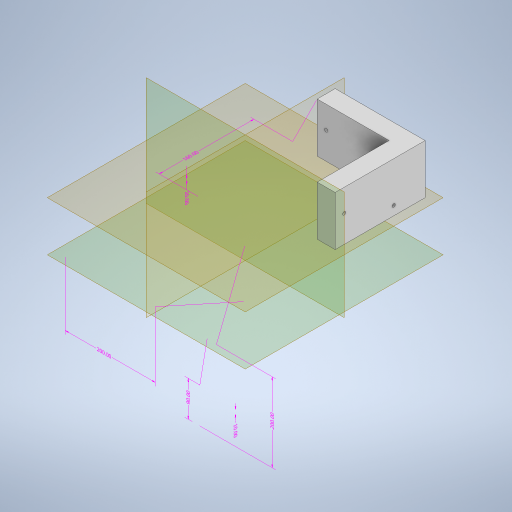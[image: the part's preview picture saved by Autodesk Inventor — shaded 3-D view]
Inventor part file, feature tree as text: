
AUTODESK INVENTOR PART (.ipt)
format: ipt  version: 2023 (Build 270158000, 158)  size: 439,808 bytes
history: native  units: mm
features: sketch x9, other x8, extrude x5, hole x4, plane x4, split x4
ambient origin geometry x8: Origin, YZ Plane, XZ Plane, XY Plane, X Axis, Y Axis, Z Axis, Center Point
bodies: Body1 (feature_tree)
feature tree (34):
  other  "Sólido1"
  other  "Anotaciones"
  extrude  "Extrusión1"  Depth=200.0mm
  hole  "Agujero1"  [1 undecoded]
  extrude  "Extrusión2"  Depth=15.0mm
  extrude  "Extrusión3"  Depth=80.0mm TaperAngle=0.0deg
  extrude  "Extrusión4"  Depth=200.0mm
  extrude  "Extrusión5"  Depth=20.0mm
  hole  "Agujero2"  [1 undecoded]
  plane  "Plano de trabajo1"
  split  "Dividir1"
  plane  "Plano de trabajo2"
  plane  "Plano de trabajo3"
  plane  "Plano de trabajo4"
  hole  "Agujero3"  [1 undecoded]
  hole  "Agujero4"  [1 undecoded]
  split  "Dividir2"
  split  "Dividir3"
  split  "Dividir4"
  sketch  "Boceto2"  dims[d7=15.0mm d8=200.0mm]
  sketch  "Boceto3"  dims[d9=10.0mm d10=0.0mm]
  sketch  "Boceto4"  dims[d11=3.5mm d12=1.75mm d13=1.75mm d14=1.75mm d15=1.75mm d16=10.0mm d17=10.0mm d19=40.0mm]
  sketch  "Boceto5"  dims[d20=3.5mm d21=6.0mm d22=4.0mm d23=2.0mm d24=90.0deg d25=8.0mm d26=20.594885mm d27=15.0mm]
  sketch  "Boceto6"  dims[d28=20.0mm d29=80.0mm d30=0.0mm]
  sketch  "Boceto7"  dims[d31=57.0mm d32=200.0mm]
  sketch  "Boceto8"  dims[d33=110.0mm d34=0.0mm d36=20.0mm]
  sketch  "Boceto9"  dims[d37=20.0mm d38=20.0mm]
  sketch  "Boceto10"  dims[d39=90.0mm d40=0.0mm d43=30.0mm d44=0.0mm d45=3.5mm d46=1.75mm d47=1.75mm d48=1.75mm d49=1.75mm d50=10.0mm d51=10.0mm d52=15.0mm d53=10.0mm d54=10.0mm d55=15.0mm d56=3.5mm d57=6.0mm d58=4.0mm d59=2.0mm d60=90.0deg d61=8.0mm d62=20.594885mm d63=10.0mm d65=10.0mm d75=200.0mm d76=10.0mm d77=20.0mm d81=40.0mm d88=90.0deg d89=10.0mm d90=30.0mm d91=5.0mm d92=5.0mm d93=5.0mm d94=5.0mm d95=30.0mm d96=5.0mm d97=5.0mm d98=3.5mm d99=5.0mm d100=5.0mm d101=5.0mm d102=5.0mm d103=5.0mm d104=20.0mm d105=3.5mm d106=6.0mm d107=4.0mm d108=2.0mm d109=90.0deg d110=8.0mm d111=20.594885mm d112=10.0mm d113=30.0mm d114=5.0mm d115=5.0mm d116=5.0mm d117=5.0mm d118=5.0mm d119=5.0mm d120=3.5mm d121=5.0mm d122=5.0mm d123=5.0mm d124=5.0mm d125=5.0mm d126=30.0mm d127=30.0mm d128=3.5mm d129=6.0mm d130=4.0mm d131=2.0mm d132=90.0deg d133=8.0mm d134=20.594885mm d66=5.760865mm d67=7.72461mm d68=200.0mm d69=3.008686mm d70=2.422102mm d71=10.0mm d72=3.500509mm d73=2.402572mm d74=90.0mm d78=3.13122mm d79=6.269346mm d80=200.0mm d82=8.450127mm d83=0.968417mm d84=20.0mm d85=4.759975mm d86=4.646891mm d87=160.0mm]
  other  "Cota lineal 1"
  other  "Cota lineal 2"
  other  "Cota lineal 3"
  other  "Cota lineal 4"
  other  "Cota lineal 5"
  other  "Cota lineal 6"
note: 4 required parameter values undecoded (feature->parameter linkage not recoverable at this tier; creation-order binding heuristic only, values carry confidence <= 0.55)
